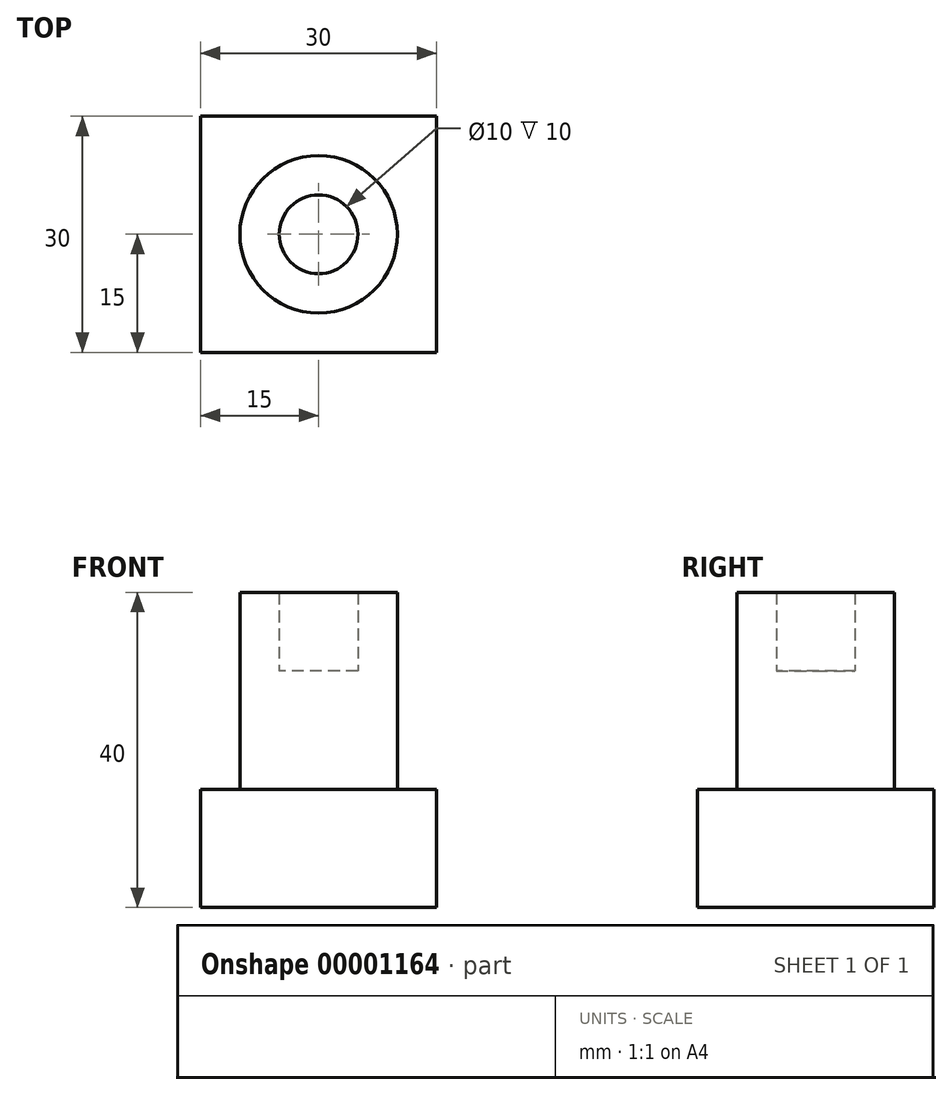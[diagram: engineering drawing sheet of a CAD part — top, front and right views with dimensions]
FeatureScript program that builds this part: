
annotation { "Feature Type Name" : "Feature", "Feature Type Description" : "" }
export const myFeature = defineFeature(function(context is Context, id is Id, definition is map)
    precondition{}
    {
        {
            var Q0;
            Q0=qCreatedBy(makeId("Top.planeOp"),FACE);
            var sketch = newSketch(context, id + "F0", { "sketchPlane" : qUnion([Q0])});
            skLineSegment(sketch, "E0.bottom", {"start": v(15, -15) * mm, "end": v(-15, -15) * mm});
            skLineSegment(sketch, "E0.top", {"start": v(15, 15) * mm, "end": v(-15, 15) * mm});
            skLineSegment(sketch, "E0.left", {"start": v(15, -15) * mm, "end": v(15, 15) * mm});
            skLineSegment(sketch, "E0.right", {"start": v(-15, -15) * mm, "end": v(-15, 15) * mm});
            skPoint(sketch, "E0.middle", {"position": v(0, 0) * mm});
            skSolve(sketch);
        }
        {
            var Q0;
            Q0 = qSketchRegion(id + "F0", true);
            extrude(context, id + "F1", {"entities" : qUnion([Q0]), "depth" : 15 * mm, "offsetDistance" : 25 * mm});
        }
        {
            var Q0;
            Q0=makeQuery(id+"F1.opExtrude","CAP_FACE",FACE,{"disambiguationData":[OSD([sQuery(id+"F0.wireOp",EDGE,"E0.bottom"),sQuery(id+"F0.wireOp",EDGE,"E0.top"),sQuery(id+"F0.wireOp",EDGE,"E0.left"),sQuery(id+"F0.wireOp",EDGE,"E0.right")])],"isStart":false});
            var sketch = newSketch(context, id + "F2", { "sketchPlane" : qUnion([Q0])});
            skCircle(sketch, "E1", {"center": v(0, 0) * mm, "radius": 10 * mm});
            skSolve(sketch);
        }
        {
            var Q0;
            Q0 = qSketchRegion(id + "F2", true);
            extrude(context, id + "F3", {"entities" : qUnion([Q0]), "operationType" : NewBodyOperationType.ADD, "depth" : 15 * mm, "offsetDistance" : 25 * mm});
        }
        {
            var Q0;
            Q0=makeQuery(id+"F3.opExtrude","CAP_FACE",FACE,{"disambiguationData":[OSD([sQuery(id+"F2.wireOp",EDGE,"E1")])],"isStart":false});
            var sketch = newSketch(context, id + "F4", { "sketchPlane" : qUnion([Q0])});
            skCircle(sketch, "E2", {"center": v(0, 0) * mm, "radius": 10 * mm});
            skCircle(sketch, "E3", {"center": v(0, 0) * mm, "radius": 5 * mm});
            skSolve(sketch);
        }
        {
            var Q0;
            Q0 = qSketchRegion(id + "F4", true);
            extrude(context, id + "F5", {"entities" : qUnion([Q0]), "operationType" : NewBodyOperationType.ADD, "depth" : 10 * mm, "offsetDistance" : 25 * mm});
        }
    });
